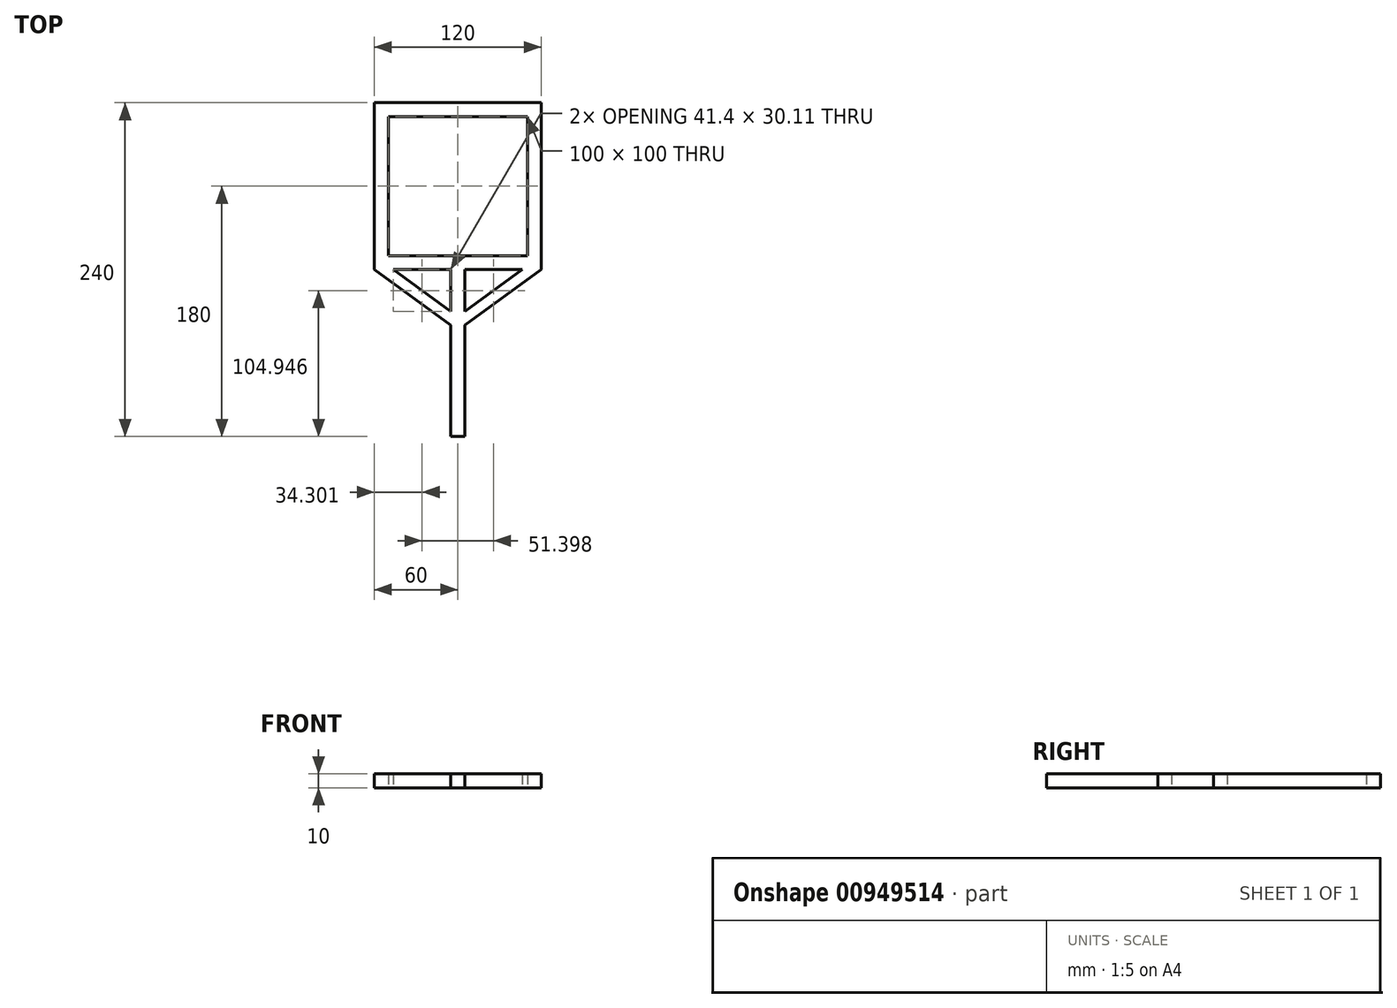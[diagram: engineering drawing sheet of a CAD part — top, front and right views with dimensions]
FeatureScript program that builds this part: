
annotation { "Feature Type Name" : "Feature", "Feature Type Description" : "" }
export const myFeature = defineFeature(function(context is Context, id is Id, definition is map)
    precondition{}
    {
        {
            var Q0;
            Q0=qCreatedBy(makeId("Front.planeOp"),FACE);
            cPlane(context, id + "F0", {"entities" : qUnion([Q0]), "cplaneType" : CPlaneType.OFFSET, "offset" : 80 * mm, "oppositeDirection" : true, "width" : 150 * mm, "height" : 150 * mm});
        }
        {
            var Q0;
            Q0=qCreatedBy(id+"F0.planeOp",FACE);
            cPlane(context, id + "F1", {"entities" : qUnion([Q0]), "cplaneType" : CPlaneType.OFFSET, "offset" : 150 * mm, "oppositeDirection" : true, "width" : 150 * mm, "height" : 150 * mm});
        }
        {
            var Q0;
            Q0=qCreatedBy(id+"F0.planeOp",FACE);
            cPlane(context, id + "F2", {"entities" : qUnion([Q0]), "cplaneType" : CPlaneType.OFFSET, "offset" : 40 * mm, "oppositeDirection" : true, "width" : 150 * mm, "height" : 150 * mm});
        }
        {
            var Q0;
            Q0=qCreatedBy(makeId("Top.planeOp"),FACE);
            var sketch = newSketch(context, id + "F3", { "sketchPlane" : qUnion([Q0])});
            skLineSegment(sketch, "E0.bottom", {"start": v(-5, 0) * mm, "end": v(5, 0) * mm});
            skLineSegment(sketch, "E0.top", {"start": v(-5, 120) * mm, "end": v(5, 120) * mm});
            skLineSegment(sketch, "E0.left", {"start": v(-5, 0) * mm, "end": v(-5, 120) * mm});
            skLineSegment(sketch, "E0.right", {"start": v(5, 0) * mm, "end": v(5, 120) * mm});
            skSolve(sketch);
        }
        {
            var Q0;
            Q0 = qSketchRegion(id + "F3", true);
            extrude(context, id + "F4", {"entities" : qUnion([Q0]), "depth" : 10 * mm, "offsetDistance" : 25 * mm});
        }
        {
            var Q0;
            Q0=qCreatedBy(makeId("Right.planeOp"),FACE);
            cPlane(context, id + "F5", {"entities" : qUnion([Q0]), "cplaneType" : CPlaneType.OFFSET, "offset" : 60 * mm, "width" : 150 * mm, "height" : 150 * mm});
        }
        {
            var Q0;
            Q0=qCreatedBy(makeId("Right.planeOp"),FACE);
            cPlane(context, id + "F6", {"entities" : qUnion([Q0]), "cplaneType" : CPlaneType.OFFSET, "offset" : 60 * mm, "oppositeDirection" : true, "width" : 150 * mm, "height" : 150 * mm});
        }
        {
            var Q0;
            Q0=qCreatedBy(makeId("Top.planeOp"),FACE);
            var sketch = newSketch(context, id + "F7", { "sketchPlane" : qUnion([Q0])});
            skLineSegment(sketch, "E1.bottom", {"start": v(-60, 130) * mm, "end": v(60, 130) * mm});
            skLineSegment(sketch, "E1.top", {"start": v(-60, 120) * mm, "end": v(60, 120) * mm});
            skLineSegment(sketch, "E1.left", {"start": v(-60, 130) * mm, "end": v(-60, 120) * mm});
            skLineSegment(sketch, "E1.right", {"start": v(60, 130) * mm, "end": v(60, 120) * mm});
            skSolve(sketch);
        }
        {
            var Q0;
            Q0 = qSketchRegion(id + "F7", true);
            extrude(context, id + "F8", {"entities" : qUnion([Q0]), "operationType" : NewBodyOperationType.ADD, "depth" : 10 * mm, "offsetDistance" : 25 * mm});
        }
        {
            var Q0;
            Q0=qCreatedBy(makeId("Top.planeOp"),FACE);
            var sketch = newSketch(context, id + "F9", { "sketchPlane" : qUnion([Q0])});
            skLineSegment(sketch, "E2.bottom", {"start": v(-60, 230) * mm, "end": v(-50, 230) * mm});
            skLineSegment(sketch, "E2.top", {"start": v(-60, 130) * mm, "end": v(-50, 130) * mm});
            skLineSegment(sketch, "E2.left", {"start": v(-60, 230) * mm, "end": v(-60, 130) * mm});
            skLineSegment(sketch, "E2.right", {"start": v(-50, 230) * mm, "end": v(-50, 130) * mm});
            skLineSegment(sketch, "E3.bottom", {"start": v(50, 230) * mm, "end": v(60, 230) * mm});
            skLineSegment(sketch, "E3.top", {"start": v(50, 130) * mm, "end": v(60, 130) * mm});
            skLineSegment(sketch, "E3.left", {"start": v(50, 230) * mm, "end": v(50, 130) * mm});
            skLineSegment(sketch, "E3.right", {"start": v(60, 230) * mm, "end": v(60, 130) * mm});
            skSolve(sketch);
        }
        {
            var Q0;
            Q0 = qSketchRegion(id + "F9", true);
            extrude(context, id + "F10", {"entities" : qUnion([Q0]), "operationType" : NewBodyOperationType.ADD, "depth" : 10 * mm, "offsetDistance" : 25 * mm});
        }
        {
            var Q0;
            Q0=qCreatedBy(makeId("Top.planeOp"),FACE);
            var sketch = newSketch(context, id + "F11", { "sketchPlane" : qUnion([Q0])});
            skLineSegment(sketch, "E4.bottom", {"start": v(-60, 240) * mm, "end": v(60, 240) * mm});
            skLineSegment(sketch, "E4.top", {"start": v(-60, 230) * mm, "end": v(60, 230) * mm});
            skLineSegment(sketch, "E4.left", {"start": v(-60, 240) * mm, "end": v(-60, 230) * mm});
            skLineSegment(sketch, "E4.right", {"start": v(60, 240) * mm, "end": v(60, 230) * mm});
            skSolve(sketch);
        }
        {
            var Q0;
            Q0 = qSketchRegion(id + "F11", true);
            extrude(context, id + "F12", {"entities" : qUnion([Q0]), "operationType" : NewBodyOperationType.ADD, "depth" : 10 * mm, "offsetDistance" : 25 * mm});
        }
        {
            var Q0;
            Q0=qCreatedBy(makeId("Top.planeOp"),FACE);
            var sketch = newSketch(context, id + "F13", { "sketchPlane" : qUnion([Q0])});
            skLineSegment(sketch, "E5", {"start": v(60, 120) * mm, "end": v(5, 80) * mm});
            skLineSegment(sketch, "E6", {"start": v(5, 80) * mm, "end": v(5, 89.9) * mm});
            skLineSegment(sketch, "E7", {"start": v(5, 89.9) * mm, "end": v(46.4, 120) * mm});
            skLineSegment(sketch, "E8", {"start": v(46.4, 120) * mm, "end": v(60, 120) * mm});
            skLineSegment(sketch, "E9", {"start": v(-5, 89.9) * mm, "end": v(-46.4, 120) * mm});
            skLineSegment(sketch, "E10", {"start": v(-46.4, 120) * mm, "end": v(-60, 120) * mm});
            skLineSegment(sketch, "E11", {"start": v(-60, 120) * mm, "end": v(-5, 80) * mm});
            skLineSegment(sketch, "E12", {"start": v(-5, 80) * mm, "end": v(-5, 89.9) * mm});
            skSolve(sketch);
        }
        {
            var Q0;
            Q0=makeQuery(id+"F13.imprint","IMPRINT",FACE,{"disambiguationData":[TD([[makeQuery(id+"F13.imprint","IMPRINT",EDGE,{"derivedFrom":sQuery(id+"F13.wireOp",EDGE,"E9")}),1.0]])]});
            var Q1;
            Q1=makeQuery(id+"F13.imprint","IMPRINT",FACE,{"disambiguationData":[TD([[makeQuery(id+"F13.imprint","IMPRINT",EDGE,{"derivedFrom":sQuery(id+"F13.wireOp",EDGE,"E5")}),-1.0]])]});
            extrude(context, id + "F14", {"entities" : qUnion([Q0, Q1]), "operationType" : NewBodyOperationType.ADD, "depth" : 10 * mm, "offsetDistance" : 25 * mm});
        }
    });
